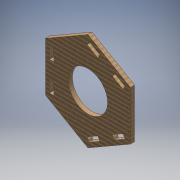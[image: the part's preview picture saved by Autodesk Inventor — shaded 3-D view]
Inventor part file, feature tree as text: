
AUTODESK INVENTOR PART (.ipt)
format: ipt  version: 2016 (Build 200138000, 138)  size: 175,104 bytes
history: native  units: mm
features: extrude x1, sketch x1
ambient origin geometry x8: Origin, YZ Plane, XZ Plane, XY Plane, X Axis, Y Axis, Z Axis, Center Point
bodies: Solid1 (feature_tree)
feature tree (2):
  extrude  "Extrusion1"  Depth=6.3261mm
  sketch  "Sketch1"  dims[d0=60.0mm d3=6.3261mm d4=18.958829mm d5=6.39mm d6=12.78mm d7=30.0mm d9=360.0deg d11=6.39mm d12=0.0mm d13=75.0mm d14=150.0mm d16=58.561905mm d17=129.903811mm]
